# Revit family: PX_FD_HERBISH_HB125HH
name_source: partatom
category: Plumbing Fixtures
revit_build: Autodesk Revit 2016 (Build: 20150220_1215(x64)
units: mm (PartAtom-declared; Revit-internal decimal feet)

## family parameters
Always vertical = Yes
Cut with Voids When Loaded = No
OmniClass Number = 23.45.55.21
OmniClass Title = Drains (Wastes)
Part Type = Normal
Room Calculation Point = No
Round Connector Dimension = Use Diameter
Shared = No
Work Plane-Based = No

## types (1)
- Herbish HB125HH
    Description = Hidden Floor Drain
    Manufacturer = Herbish® Drainage Systems
    Note 1 = Only On Special Order
    Note 2 = Manufactured in 304 and 316 grade stainless steel
    Note 3 = Supplied with a 50mm outlet but 76mm diameter outlet
    Note 4 = Supplied with strainer
    Stainless Steel = Stainless Steel
    Tile 1 = Tile 1
    Tolani Civil Projects cc URL = www.tcpbim.co.za
    URL = https://www.herbish.co.za

## geometry (parser evidence)
native form markers: Sweep x2
no freeform markers — native parametric forms only
